FCSTD DOCUMENT  (FreeCAD 1.0R39109 (Git))
Label: servo
License: All rights reserved
LicenseURL: https://en.wikipedia.org/wiki/All_rights_reserved
objects: Sketcher::SketchObject×1, PartDesign::Body×1
note: 3 computed .brp shape members not serialized (recipe doc carries the construction recipe); baked Part::Feature solids carry a one-line shape summary decoded from their .brp

FEATURE [Sketcher::SketchObject] Sketch
  ArcFitTolerance = 1e-06
  AttachmentSupport = -> [XY_Plane]
  FullyConstrained = false
  MakeInternals = false
  MapMode = 5
  sketch-geometry (32):
    g0: LineSegment StartX=0 StartY=0 StartZ=0 EndX=40.2 EndY=0 EndZ=0
    g1: LineSegment StartX=40.2 StartY=0 StartZ=0 EndX=40.2 EndY=61.1 EndZ=0
    g2: LineSegment StartX=40.2 StartY=61.1 StartZ=0 EndX=0 EndY=61.1 EndZ=0
    g3: LineSegment StartX=0 StartY=61.1 StartZ=0 EndX=0 EndY=0 EndZ=0
    g4: LineSegment [constr] StartX=20.1 StartY=61.1 StartZ=0 EndX=20.1 EndY=48.1 EndZ=0
    g5: Circle CenterX=20.1 CenterY=48.1 CenterZ=0 NormalX=0 NormalY=0 NormalZ=1 AngleXU=0 Radius=14
    g6: LineSegment [constr] StartX=20.1 StartY=48.1 StartZ=0 EndX=20.1 EndY=5.6 EndZ=0
    g7: Circle [constr] CenterX=20.1 CenterY=5.6 CenterZ=0 NormalX=0 NormalY=0 NormalZ=1 AngleXU=0 Radius=14.5
    g8: LineSegment [constr] StartX=20.1 StartY=5.6 StartZ=0 EndX=34.6 EndY=5.6 EndZ=0
    g9: LineSegment StartX=34.6 StartY=5.6 StartZ=0 EndX=5.6 EndY=5.6 EndZ=0
    g10: LineSegment StartX=5.6 StartY=5.6 StartZ=0 EndX=5.6 EndY=61.1 EndZ=0
    g11: LineSegment StartX=34.6 StartY=5.6 StartZ=0 EndX=34.6 EndY=61.1 EndZ=0
    g12: LineSegment [constr] StartX=20.1 StartY=48.1 StartZ=0 EndX=20.1 EndY=2.8 EndZ=0
    g13: Circle [constr] CenterX=20.1 CenterY=2.8 CenterZ=0 NormalX=0 NormalY=0 NormalZ=1 AngleXU=0 Radius=11
    g14: LineSegment [constr] StartX=20.1 StartY=2.8 StartZ=0 EndX=9.1 EndY=2.8 EndZ=0
    g15: LineSegment [constr] StartX=20.1 StartY=2.8 StartZ=0 EndX=31.1 EndY=2.8 EndZ=0
    g16: Circle CenterX=31.1 CenterY=2.8 CenterZ=0 NormalX=0 NormalY=0 NormalZ=1 AngleXU=0 Radius=1.25
    g17: Circle CenterX=9.1 CenterY=2.8 CenterZ=0 NormalX=0 NormalY=0 NormalZ=1 AngleXU=0 Radius=1.25
    g18: LineSegment [constr] StartX=20.1 StartY=48.1 StartZ=0 EndX=20.1 EndY=52.1 EndZ=0
    g19: Circle [constr] CenterX=20.1 CenterY=52.1 CenterZ=0 NormalX=0 NormalY=0 NormalZ=1 AngleXU=0 Radius=17.3
    g20: LineSegment [constr] StartX=20.1 StartY=52.1 StartZ=0 EndX=2.8 EndY=52.1 EndZ=0
    g21: LineSegment [constr] StartX=20.1 StartY=52.1 StartZ=0 EndX=37.4 EndY=52.1 EndZ=0
    g22: Circle CenterX=2.8 CenterY=52.1 CenterZ=0 NormalX=0 NormalY=0 NormalZ=1 AngleXU=0 Radius=1.25
    g23: Circle CenterX=37.4 CenterY=52.1 CenterZ=0 NormalX=0 NormalY=0 NormalZ=1 AngleXU=0 Radius=1.25
    g24: LineSegment [constr] StartX=37.4 StartY=52.1 StartZ=0 EndX=37.4 EndY=30.1 EndZ=0
    g25: LineSegment [constr] StartX=37.4 StartY=30.1 StartZ=0 EndX=37.4 EndY=8.1 EndZ=0
    g26: LineSegment [constr] StartX=2.8 StartY=52.1 StartZ=0 EndX=2.8 EndY=30.1 EndZ=0
    g27: LineSegment [constr] StartX=2.8 StartY=30.1 StartZ=0 EndX=2.8 EndY=8.1 EndZ=0
    g28: Circle CenterX=2.8 CenterY=30.1 CenterZ=0 NormalX=0 NormalY=0 NormalZ=1 AngleXU=0 Radius=1.25
    g29: Circle CenterX=2.8 CenterY=8.1 CenterZ=0 NormalX=0 NormalY=0 NormalZ=1 AngleXU=0 Radius=1.25
    g30: Circle CenterX=37.4 CenterY=30.1 CenterZ=0 NormalX=0 NormalY=0 NormalZ=1 AngleXU=0 Radius=1.25
    g31: Circle CenterX=37.4 CenterY=8.1 CenterZ=0 NormalX=0 NormalY=0 NormalZ=1 AngleXU=0 Radius=1.25
  constraints (81):
    c: Coincident(g0,g1)
    c: Coincident(g1,g2)
    c: Coincident(g2,g3)
    c: Coincident(g3,g0)
    c: Horizontal(g0)
    c: Horizontal(g2)
    c: Vertical(g1)
    c: Vertical(g3)
    c: Distance(g1,g3) = 40.2
    c: Distance(g0,g2) = 61.1
    c: Coincident(g0,g-1)
    c: Distance(g4) = 13
    c: Symmetric(g2,g2,g4)
    c: Vertical(g4)
    c: Diameter(g5) = 28
    c: Coincident(g5,g4)
    c: Distance(g6) = 42.5
    c: Coincident(g6,g4)
    c: Vertical(g6)
    c: Diameter(g7) = 29
    c: Coincident(g7,g6)
    c: Coincident(g8,g6)
    c: PointOnObject(g8,g7)
    c: Horizontal(g8)
    c: Coincident(g9,g8)
    c: PointOnObject(g9,g7)
    c: Horizontal(g9)
    c: Coincident(g10,g9)
    c: PointOnObject(g10,g2)
    c: Vertical(g10)
    c: Coincident(g11,g8)
    c: PointOnObject(g11,g2)
    c: Vertical(g11)
    c: Distance(g12) = 45.3
    c: Coincident(g12,g4)
    c: Vertical(g12)
    c: Diameter(g13) = 22
    c: Coincident(g13,g12)
    c: Coincident(g14,g12)
    c: PointOnObject(g14,g13)
    c: Horizontal(g14)
    c: Coincident(g15,g12)
    c: PointOnObject(g15,g13)
    c: Horizontal(g15)
    c: Diameter(g16) = 2.5
    c: Coincident(g16,g15)
    c: Coincident(g17,g14)
    c: Equal(g16,g17)
    c: Distance(g18) = 4
    c: Coincident(g18,g4)
    c: PointOnObject(g18,g4)
    c: Diameter(g19) = 34.6
    c: Coincident(g19,g18)
    c: Coincident(g20,g18)
    c: PointOnObject(g20,g19)
    c: Horizontal(g20)
    c: Coincident(g22,g20)
    c: Coincident(g23,g21)
    c: Equal(g16,g23)
    c: Equal(g16,g22)
    c: Distance(g24) = 22
    c: Vertical(g24)
    c: Coincident(g24,g21)
    c: Tangent(g24,g19)
    c: Distance(g25) = 22
    c: Vertical(g25)
    c: Coincident(g25,g24)
    c: Distance(g26) = 22
    c: Coincident(g26,g20)
    c: Vertical(g26)
    c: Distance(g27) = 22
    c: Coincident(g27,g26)
    c: Vertical(g27)
    c: Coincident(g28,g26)
    c: Coincident(g29,g27)
    c: Equal(g16,g28)
    c: Equal(g16,g29)
    c: Coincident(g30,g24)
    c: Coincident(g31,g25)
    c: Equal(g16,g31)
    c: Equal(g16,g30)
FEATURE [PartDesign::Body] Body
  AllowCompound = false
  Group = -> [Sketch]
  Origin = -> Origin
